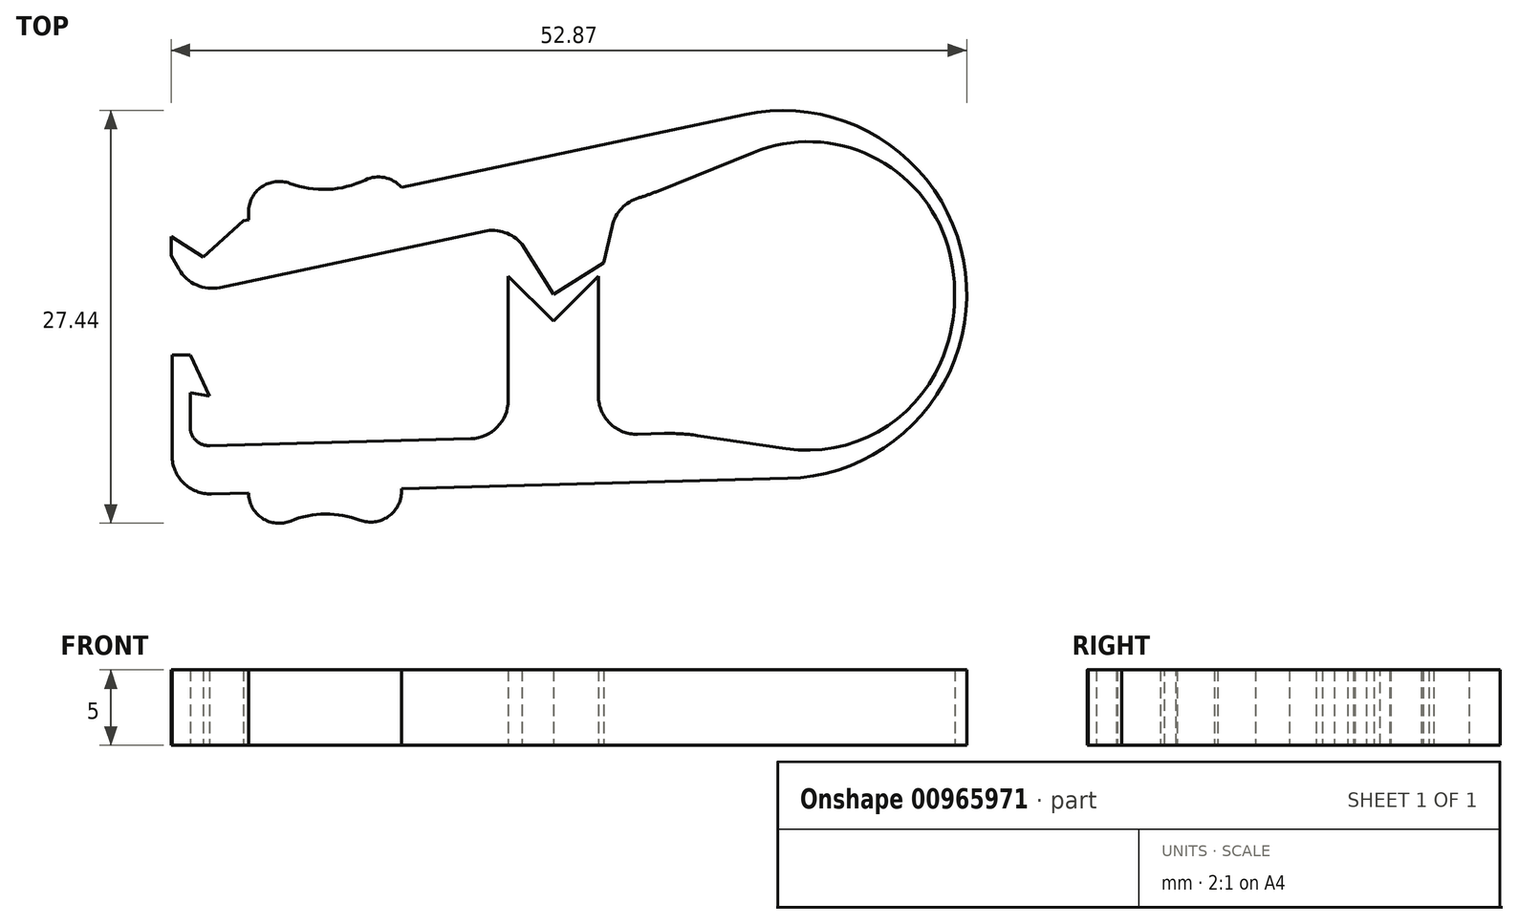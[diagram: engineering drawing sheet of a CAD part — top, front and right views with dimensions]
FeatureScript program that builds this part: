
annotation { "Feature Type Name" : "Feature", "Feature Type Description" : "" }
export const myFeature = defineFeature(function(context is Context, id is Id, definition is map)
    precondition{}
    {
        {
            var Q0;
            Q0=qCreatedBy(makeId("Top.planeOp"),FACE);
            var sketch = newSketch(context, id + "F0", { "sketchPlane" : qUnion([Q0])});
            skArc(sketch, "E0", {"start": v(8.48, -9.21) * mm, "mid": v(26.5, 1.95) * mm, "end": v(5.77, 6.4) * mm});
            skArc(sketch, "E1", {"start": v(15.57, -12.23) * mm, "mid": v(27.38, 1.44) * mm, "end": v(12.7, 11.96) * mm});
            skLineSegment(sketch, "E2", {"start": v(12.7, 11.96) * mm, "end": v(-25.4, 3.86) * mm});
            skLineSegment(sketch, "E3", {"start": v(15.57, -12.23) * mm, "end": v(-25.33, -13.32) * mm});
            skLineSegment(sketch, "E4", {"start": v(-25.33, -13.32) * mm, "end": v(-25.33, -4.03) * mm});
            skLineSegment(sketch, "E5", {"start": v(-25.33, -4.03) * mm, "end": v(-24.13, -4.03) * mm});
            skLineSegment(sketch, "E6", {"start": v(-24.13, -4.03) * mm, "end": v(-24.13, -10.1) * mm});
            skLineSegment(sketch, "E7", {"start": v(-24.13, -10.1) * mm, "end": v(8.48, -9.21) * mm});
            skLineSegment(sketch, "E8", {"start": v(-3, -9.52) * mm, "end": v(-3, 1.22) * mm});
            skLineSegment(sketch, "E9", {"start": v(-3, 1.22) * mm, "end": v(0, -1.78) * mm});
            skLineSegment(sketch, "E10", {"start": v(0, -1.78) * mm, "end": v(3, 1.22) * mm});
            skLineSegment(sketch, "E11", {"start": v(3, 1.22) * mm, "end": v(3, -9.36) * mm});
            skLineSegment(sketch, "E12", {"start": v(-0.77, 9.1) * mm, "end": v(-2.1, 3.35) * mm});
            skLineSegment(sketch, "E13", {"start": v(-2.1, 3.35) * mm, "end": v(0, 0) * mm});
            skLineSegment(sketch, "E14", {"start": v(0, 0) * mm, "end": v(3.35, 2.1) * mm});
            skLineSegment(sketch, "E15", {"start": v(3.35, 2.1) * mm, "end": v(5.26, 10.38) * mm});
            skLineSegment(sketch, "E16", {"start": v(-25.4, 3.86) * mm, "end": v(-25.4, -0.22) * mm});
            skLineSegment(sketch, "E17", {"start": v(-25.4, -0.22) * mm, "end": v(-1.76, 4.8) * mm});
            skLineSegment(sketch, "E18", {"start": v(4.27, 6.08) * mm, "end": v(5.77, 6.4) * mm});
            skLineSegment(sketch, "E19", {"start": v(-24.13, -4.03) * mm, "end": v(-22.86, -6.76) * mm});
            skLineSegment(sketch, "E20", {"start": v(-22.86, -6.76) * mm, "end": v(-24.13, -6.53) * mm});
            skLineSegment(sketch, "E21", {"start": v(-25.4, 3.86) * mm, "end": v(-23.27, 2.48) * mm});
            skLineSegment(sketch, "E22", {"start": v(-23.27, 2.48) * mm, "end": v(-20.6, 4.89) * mm});
            skLineSegment(sketch, "E23", {"start": v(0, -1.78) * mm, "end": v(0, 0) * mm, "construction": true});
            skLineSegment(sketch, "E24", {"start": v(-25.4, 2.6) * mm, "end": v(-23.95, 0.08) * mm});
            skLineSegment(sketch, "E25", {"start": v(8.48, -9.21) * mm, "end": v(19.03, -10.78) * mm});
            skLineSegment(sketch, "E26", {"start": v(5.77, 6.4) * mm, "end": v(17.6, 11.18) * mm});
            skLineSegment(sketch, "E27", {"start": v(-20.25, 4.96) * mm, "end": v(-20.25, 9.39) * mm});
            skLineSegment(sketch, "E28", {"start": v(-10.1, 9.66) * mm, "end": v(-10.1, 7.12) * mm});
            skArc(sketch, "E29", {"start": v(-20.25, 9.39) * mm, "mid": v(-15.1, 6.98) * mm, "end": v(-10.1, 9.66) * mm});
            skLineSegment(sketch, "E30", {"start": v(-20.25, -13.19) * mm, "end": v(-20.25, -17.27) * mm});
            skArc(sketch, "E31", {"start": v(-10.09, -17) * mm, "mid": v(-15.24, -14.6) * mm, "end": v(-20.25, -17.27) * mm});
            skLineSegment(sketch, "E32", {"start": v(-10.1, -12.91) * mm, "end": v(-10.09, -17) * mm});
            skLineSegment(sketch, "E33", {"start": v(-20.25, -17.27) * mm, "end": v(-10.09, -17) * mm, "construction": true});
            skLineSegment(sketch, "E34", {"start": v(-20.25, 9.39) * mm, "end": v(-10.1, 9.66) * mm, "construction": true});
            skSolve(sketch);
        }
        {
            var Q0;
            {var subQ0=sQuery(id+"F0.wireOp",EDGE,"E13");Q0=makeQuery(id+"F0.imprint","IMPRINT",FACE,{"disambiguationData":[TD([[makeQuery(id+"F0.imprint","IMPRINT",EDGE,{"derivedFrom":subQ0}),1.0]])]});}
            var Q1;
            {var subQ6=sQuery(id+"F0.wireOp",EDGE,"E0");Q1=makeQuery(id+"F0.imprint","IMPRINT",FACE,{"disambiguationData":[TD([[makeQuery(id+"F0.imprint","IMPRINT",EDGE,{"derivedFrom":subQ6}),-1.0]])]});}
            var Q2;
            {var subQ0=sQuery(id+"F0.wireOp",EDGE,"E19");Q2=makeQuery(id+"F0.imprint","IMPRINT",FACE,{"disambiguationData":[TD([[makeQuery(id+"F0.imprint","IMPRINT",EDGE,{"derivedFrom":subQ0}),-1.0]])]});}
            var Q3;
            {var subQ0=sQuery(id+"F0.wireOp",EDGE,"E8");Q3=makeQuery(id+"F0.imprint","IMPRINT",FACE,{"disambiguationData":[TD([[makeQuery(id+"F0.imprint","IMPRINT",EDGE,{"derivedFrom":subQ0}),-1.0]])]});}
            var Q4;
            {var subQ6=sQuery(id+"F0.wireOp",EDGE,"E21");Q4=makeQuery(id+"F0.imprint","IMPRINT",FACE,{"disambiguationData":[TD([[makeQuery(id+"F0.imprint","IMPRINT",EDGE,{"derivedFrom":subQ6}),-1.0]])]});}
            var Q5;
            {var subQ0=sQuery(id+"F0.wireOp",EDGE,"E26");Q5=makeQuery(id+"F0.imprint","IMPRINT",FACE,{"disambiguationData":[TD([[makeQuery(id+"F0.imprint","IMPRINT",EDGE,{"derivedFrom":subQ0}),1.0]])]});}
            var Q6;
            {var subQ0=sQuery(id+"F0.wireOp",EDGE,"E25");Q6=makeQuery(id+"F0.imprint","IMPRINT",FACE,{"disambiguationData":[TD([[makeQuery(id+"F0.imprint","IMPRINT",EDGE,{"derivedFrom":subQ0}),-1.0]])]});}
            var Q7;
            {var subQ0=sQuery(id+"F0.wireOp",EDGE,"E27");Q7=makeQuery(id+"F0.imprint","IMPRINT",FACE,{"disambiguationData":[TD([[makeQuery(id+"F0.imprint","IMPRINT",EDGE,{"derivedFrom":subQ0}),-1.0]])]});}
            var Q8;
            {var subQ0=sQuery(id+"F0.wireOp",EDGE,"E30");Q8=makeQuery(id+"F0.imprint","IMPRINT",FACE,{"disambiguationData":[TD([[makeQuery(id+"F0.imprint","IMPRINT",EDGE,{"derivedFrom":subQ0}),1.0]])]});}
            extrude(context, id + "F1", {"entities" : qUnion([Q0, Q1, Q2, Q3, Q4, Q5, Q6, Q7, Q8]), "depth" : 5 * mm, "offsetDistance" : 25.4 * mm});
        }
        {
            var Q0;
            Q0=makeQuery(id+"F1.opExtrude","SWEPT_EDGE",EDGE,{"disambiguationData":[OSD([sQuery(id+"F0.wireOp",EDGE,"E0"),sQuery(id+"F0.wireOp",EDGE,"E18")])]});
            var Q1;
            Q1=makeQuery(id+"F1.opExtrude","SWEPT_EDGE",EDGE,{"disambiguationData":[OSD([sQuery(id+"F0.wireOp",EDGE,"E0"),sQuery(id+"F0.wireOp",EDGE,"E7")])]});
            fillet(context, id + "F2", {"entities" : qUnion([Q0, Q1]), "radius" : 12.7 * mm, "tangentPropagation" : true, "allowEdgeOverflow" : false});
        }
        {
            var Q0;
            Q0=makeQuery(id+"F1.opExtrude","SWEPT_EDGE",EDGE,{"disambiguationData":[OSD([sQuery(id+"F0.wireOp",EDGE,"E15"),sQuery(id+"F0.wireOp",EDGE,"E18")])]});
            var Q1;
            Q1=makeQuery(id+"F1.opExtrude","SWEPT_EDGE",EDGE,{"disambiguationData":[OSD([sQuery(id+"F0.wireOp",EDGE,"E7"),sQuery(id+"F0.wireOp",EDGE,"E11")])]});
            var Q2;
            Q2=makeQuery(id+"F1.opExtrude","SWEPT_EDGE",EDGE,{"disambiguationData":[OSD([sQuery(id+"F0.wireOp",EDGE,"E7"),sQuery(id+"F0.wireOp",EDGE,"E8")])]});
            var Q3;
            Q3=makeQuery(id+"F1.opExtrude","SWEPT_EDGE",EDGE,{"disambiguationData":[OSD([sQuery(id+"F0.wireOp",EDGE,"E12"),sQuery(id+"F0.wireOp",EDGE,"E17")])]});
            var Q4;
            Q4=makeQuery(id+"F1.opExtrude","SWEPT_EDGE",EDGE,{"disambiguationData":[OSD([sQuery(id+"F0.wireOp",EDGE,"E3"),sQuery(id+"F0.wireOp",EDGE,"E4")])]});
            var Q5;
            Q5=makeQuery(id+"F2.opFillet","BLEND_EDGE",EDGE,{"blendedFrom":[makeQuery(id+"F1.opExtrude","SWEPT_EDGE",EDGE,{"disambiguationData":[OSD([sQuery(id+"F0.wireOp",EDGE,"E0"),sQuery(id+"F0.wireOp",EDGE,"E18"),sQuery(id+"F0.wireOp",EDGE,"E26")])]}),makeQuery(id+"F1.opExtrude","SWEPT_FACE",FACE,{"disambiguationData":[OSD([sQuery(id+"F0.wireOp",EDGE,"E15")])]})],"blendedInto":[makeQuery(id+"F1.opExtrude","SWEPT_FACE",FACE,{"disambiguationData":[OSD([sQuery(id+"F0.wireOp",EDGE,"E15")])]})]});
            var Q6;
            {var subQ0=sQuery(id+"F0.wireOp",EDGE,"E26");Q6=makeQuery(id+"F2.opFillet","BLEND_EDGE",EDGE,{"blendedFrom":[makeQuery(id+"F1.opExtrude","SWEPT_EDGE",EDGE,{"disambiguationData":[OSD([sQuery(id+"F0.wireOp",EDGE,"E0"),sQuery(id+"F0.wireOp",EDGE,"E18"),subQ0])]}),makeQuery(id+"F1.opExtrude","SWEPT_FACE",FACE,{"disambiguationData":[OSD([subQ0])]})],"blendedInto":[makeQuery(id+"F1.opExtrude","SWEPT_FACE",FACE,{"disambiguationData":[OSD([subQ0])]})]});}
            var Q7;
            {var subQ0=sQuery(id+"F0.wireOp",EDGE,"E25");Q7=makeQuery(id+"F2.opFillet","BLEND_EDGE",EDGE,{"blendedFrom":[makeQuery(id+"F1.opExtrude","SWEPT_EDGE",EDGE,{"disambiguationData":[OSD([sQuery(id+"F0.wireOp",EDGE,"E0"),sQuery(id+"F0.wireOp",EDGE,"E7"),subQ0])]}),makeQuery(id+"F1.opExtrude","SWEPT_FACE",FACE,{"disambiguationData":[OSD([subQ0])]})],"blendedInto":[makeQuery(id+"F1.opExtrude","SWEPT_FACE",FACE,{"disambiguationData":[OSD([subQ0])]})]});}
            var Q8;
            Q8=makeQuery(id+"F1.opExtrude","SWEPT_EDGE",EDGE,{"disambiguationData":[OSD([sQuery(id+"F0.wireOp",EDGE,"E17"),sQuery(id+"F0.wireOp",EDGE,"E24")])]});
            fillet(context, id + "F3", {"entities" : qUnion([Q0, Q1, Q2, Q3, Q4, Q5, Q6, Q7, Q8]), "radius" : 2.54 * mm, "tangentPropagation" : true, "allowEdgeOverflow" : false});
        }
        {
            var Q0;
            Q0=makeQuery(id+"F1.opExtrude","SWEPT_EDGE",EDGE,{"disambiguationData":[OSD([sQuery(id+"F0.wireOp",EDGE,"E6"),sQuery(id+"F0.wireOp",EDGE,"E7")])]});
            fillet(context, id + "F4", {"entities" : qUnion([Q0]), "radius" : 1.27 * mm, "tangentPropagation" : true, "allowEdgeOverflow" : false});
        }
        {
            var Q0;
            Q0=makeQuery(id+"F1.opExtrude","SWEPT_EDGE",EDGE,{"disambiguationData":[OSD([sQuery(id+"F0.wireOp",EDGE,"E0"),sQuery(id+"F0.wireOp",EDGE,"E26")])]});
            var Q1;
            Q1=makeQuery(id+"F1.opExtrude","SWEPT_EDGE",EDGE,{"disambiguationData":[OSD([sQuery(id+"F0.wireOp",EDGE,"E0"),sQuery(id+"F0.wireOp",EDGE,"E25")])]});
            fillet(context, id + "F5", {"entities" : qUnion([Q0, Q1]), "radius" : 9.65 * mm, "tangentPropagation" : true, "allowEdgeOverflow" : false});
        }
        {
            var Q0;
            Q0=makeQuery(id+"F1.opExtrude","SWEPT_EDGE",EDGE,{"disambiguationData":[OSD([sQuery(id+"F0.wireOp",EDGE,"E27"),sQuery(id+"F0.wireOp",EDGE,"E29")])]});
            var Q1;
            Q1=makeQuery(id+"F1.opExtrude","SWEPT_EDGE",EDGE,{"disambiguationData":[OSD([sQuery(id+"F0.wireOp",EDGE,"E28"),sQuery(id+"F0.wireOp",EDGE,"E29")])]});
            var Q2;
            Q2=makeQuery(id+"F1.opExtrude","SWEPT_EDGE",EDGE,{"disambiguationData":[OSD([sQuery(id+"F0.wireOp",EDGE,"E31"),sQuery(id+"F0.wireOp",EDGE,"E32")])]});
            var Q3;
            Q3=makeQuery(id+"F1.opExtrude","SWEPT_EDGE",EDGE,{"disambiguationData":[OSD([sQuery(id+"F0.wireOp",EDGE,"E30"),sQuery(id+"F0.wireOp",EDGE,"E31")])]});
            fillet(context, id + "F6", {"entities" : qUnion([Q0, Q1, Q2, Q3]), "tangentPropagation" : true, "radius" : 2.03 * mm, "defaultsChanged" : true, "vertexSettings" : [], "allowEdgeOverflow" : false});
        }
    });
